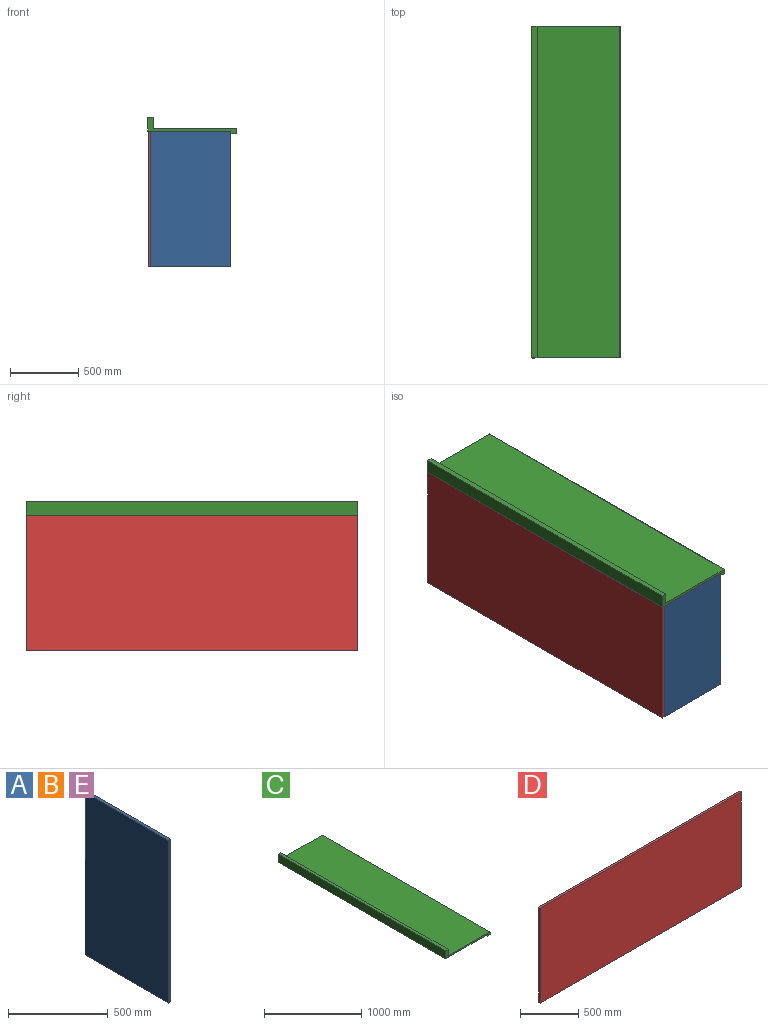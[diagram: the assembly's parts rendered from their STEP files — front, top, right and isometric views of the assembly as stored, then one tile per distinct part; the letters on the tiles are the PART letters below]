
ASSEMBLY  parts=5 mates=4
PART A: 6 faces, bbox 19.1x590.6x997 mm
  f0: plane 996.95x19.05mm, normal (0,1,0), area 18991.9mm2, adj f1,f3,f4,f5
  f1: plane 996.95x590.55mm, normal (-1,0,0), area 588748.8mm2, adj f0,f2,f4,f5
  f2: plane 996.95x19.05mm, normal (0,-1,0), area 18991.9mm2, adj f1,f3,f4,f5
  f3: plane 996.95x590.55mm, normal (1,0,0), area 588748.8mm2, adj f0,f2,f4,f5
  f4: plane 590.55x19.05mm, normal (0,0,1), area 11250mm2, adj f0,f1,f2,f3
  f5: plane 590.55x19.05mm, normal (0,0,-1), area 11250mm2, adj f0,f1,f2,f3
PART B: same geometry as A
PART C: 11 faces, bbox 649.2x2438.4x120.7 mm
  f0: plane 2438.4x19.05mm, normal (-1,0,0), area 46451.5mm2, adj f1,f2,f6,f7
  f1: plane 649.22x120.65mm, normal (0,1,0), area 16233.1mm2, adj f0,f3,f4,f5,f6,f7,f8,f9
  f2: plane 649.22x120.65mm, normal (0,-1,0), area 16233.1mm2, adj f0,f3,f4,f5,f6,f7,f8,f9
  f3: plane 2438.4x33.02mm, normal (1,0,0), area 80516mm2, adj f1,f2,f5,f6
  f4: plane 2438.4x606.04mm, normal (0,0,1), area 1477777.7mm2, adj f1,f2,f5,f8
  f5: cylinder r=5.08mm len=2438.4mm, axis (0,-1,0), area 19457.6mm2, adj f1,f2,f3,f4
  f6: plane 2438.4x38.1mm, normal (0,0,-1), area 92903mm2, adj f0,f1,f2,f3
  f7: plane 2438.4x611.12mm, normal (0,0,-1), area 1490164.8mm2, adj f0,f1,f2,f9
  f8: plane 2438.4x82.55mm, normal (1,0,0), area 201289.9mm2, adj f1,f2,f4,f10
  f9: plane 2438.4x101.6mm, normal (-1,0,0), area 247741.4mm2, adj f1,f2,f7,f10
  f10: plane 2438.4x38.1mm, normal (0,0,1), area 92903mm2, adj f1,f2,f8,f9
PART D: 6 faces, bbox 2438.4x19.1x997 mm
  f0: plane 996.95x19.05mm, normal (-1,0,0), area 18991.9mm2, adj f1,f3,f4,f5
  f1: plane 2438.4x19.05mm, normal (0,0,-1), area 46451.5mm2, adj f0,f2,f4,f5
  f2: plane 996.95x19.05mm, normal (1,0,0), area 18991.9mm2, adj f1,f3,f4,f5
  f3: plane 2438.4x19.05mm, normal (0,0,1), area 46451.5mm2, adj f0,f2,f4,f5
  f4: plane 2438.4x996.95mm, normal (0,-1,0), area 2430962.9mm2, adj f0,f1,f2,f3
  f5: plane 2438.4x996.95mm, normal (0,1,0), area 2430962.9mm2, adj f0,f1,f2,f3
PART E: same geometry as A
PLACE A rot(axis=(0,0,1),90deg) t=(231.46,-38.76,-996.95)mm
PLACE B rot(axis=(0,0,-1),90deg) t=(-234.23,1189.97,-996.95)mm
PLACE C at identity
PLACE D rot(axis=(0,0,-1),90deg) t=(-296.66,1228.07,-412.79)mm
PLACE E rot(axis=(0,0,-1),90deg) t=(-234.23,2399.64,-996.95)mm
MATE fastened B.f4 <-> C.f7  axis (0,0,1) through (293.89,1180.44,0)mm
MATE fastened D.f5 <-> B.f2  axis (1,0,0) through (-296.66,1180.44,-498.48)mm
MATE fastened A.f4 <-> C.f7  axis (0,0,1) through (293.89,-38.76,0)mm
MATE fastened E.f4 <-> C.f7  axis (0,0,1) through (293.89,2399.64,0)mm
